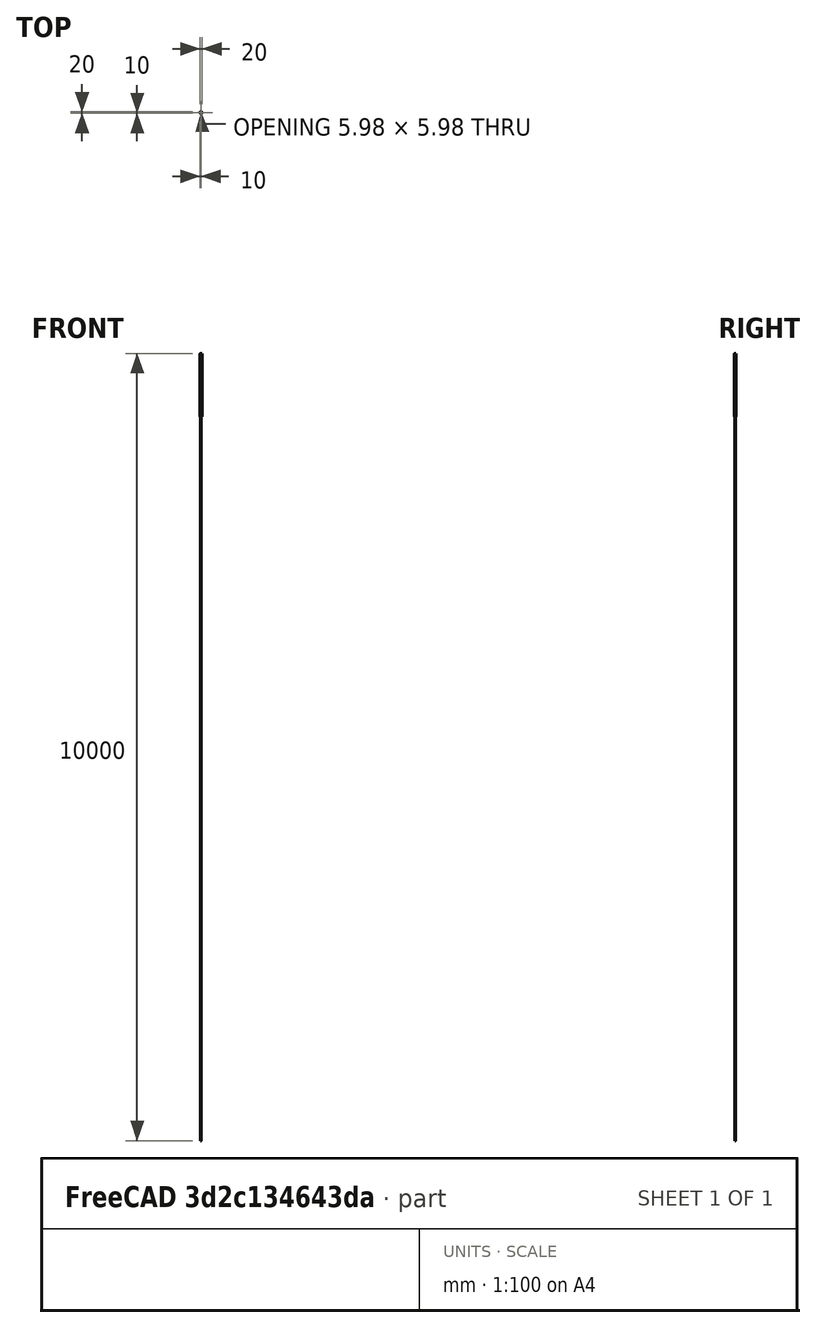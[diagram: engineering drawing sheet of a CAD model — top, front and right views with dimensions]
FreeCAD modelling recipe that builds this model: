
FCSTD DOCUMENT  (FreeCAD 0.14R3703 (Git))
Label: perfiles_verticales
License: CC-BY 3.0
LicenseURL: http://creativecommons.org/licenses/by/3.0/
objects: Sketcher::SketchObject×2, PartDesign::Pad×1, PartDesign::Pocket×1, Part::Feature×1
note: 7 computed .brp shape members not serialized (recipe doc carries the construction recipe); baked Part::Feature solids carry a one-line shape summary decoded from their .brp

FEATURE [Sketcher::SketchObject] Sketch
  Placement = pos=(1.5,0,0) rot=(0,0,1;0rad)
  sketch-geometry (136):
    g0: LineSegment StartX=0 StartY=20 StartZ=0 EndX=4.65 EndY=20 EndZ=0
    g1: ArcOfCircle CenterX=-1e-12 CenterY=18.5 CenterZ=0 NormalX=0 NormalY=0 NormalZ=1 Radius=1.5 StartAngle=1.5708 EndAngle=3.14159
    g2: LineSegment StartX=-1.5 StartY=13.85 StartZ=0 EndX=-1.5 EndY=18.5 EndZ=0
    g3: ArcOfCircle CenterX=-1.3 CenterY=13.85 CenterZ=0 NormalX=0 NormalY=0 NormalZ=1 Radius=0.2 StartAngle=3.14159 EndAngle=4.71239
    g4: LineSegment StartX=-1 StartY=13.65 StartZ=0 EndX=-1.3 EndY=13.65 EndZ=0
    g5: LineSegment StartX=-1 StartY=13.3 StartZ=0 EndX=-1 EndY=13.65 EndZ=0
    g6: ArcOfCircle CenterX=-0.8 CenterY=13.3 CenterZ=0 NormalX=0 NormalY=0 NormalZ=1 Radius=0.2 StartAngle=3.14159 EndAngle=4.71239
    g7: LineSegment StartX=-0.5 StartY=13.1 StartZ=0 EndX=-0.8 EndY=13.1 EndZ=0
    g8: ArcOfCircle CenterX=-0.5 CenterY=13.6 CenterZ=0 NormalX=0 NormalY=0 NormalZ=1 Radius=0.5 StartAngle=4.71239 EndAngle=6.28319
    g9: LineSegment StartX=2.68e-07 StartY=15.5 StartZ=0 EndX=2.68e-07 EndY=13.6 EndZ=0
    g10: ArcOfCircle CenterX=0.5 CenterY=15.5 CenterZ=0 NormalX=0 NormalY=0 NormalZ=1 Radius=0.5 StartAngle=1.5708 EndAngle=3.14159
    g11: LineSegment StartX=1.23223 StartY=16 StartZ=0 EndX=0.5 EndY=16 EndZ=0
    g12: ArcOfCircle CenterX=1.23223 CenterY=15.5 CenterZ=0 NormalX=0 NormalY=0 NormalZ=1 Radius=0.5 StartAngle=0.785398 EndAngle=1.5708
    g13: LineSegment StartX=3.85355 StartY=13.5858 StartZ=0 EndX=1.58579 EndY=15.8536 EndZ=0
    g14: ArcOfCircle CenterX=3.5 CenterY=13.2322 CenterZ=0 NormalX=0 NormalY=0 NormalZ=1 Radius=0.5 StartAngle=0 EndAngle=0.785398
    g15: LineSegment StartX=4 StartY=10.9536 StartZ=0 EndX=4 EndY=13.2322 EndZ=0
    g16: ArcOfCircle CenterX=4.2 CenterY=10.9536 CenterZ=0 NormalX=0 NormalY=0 NormalZ=1 Radius=0.2 StartAngle=3.14159 EndAngle=3.66519
    g17: LineSegment StartX=4.46188 StartY=10.1 StartZ=0 EndX=4.0268 EndY=10.8536 EndZ=0
    g18: ArcOfCircle CenterX=4.28868 CenterY=10 CenterZ=0 NormalX=0 NormalY=0 NormalZ=1 Radius=0.2 StartAngle=5.75959 EndAngle=6.80678
    g19: LineSegment StartX=4.0268 StartY=9.14641 StartZ=0 EndX=4.46188 EndY=9.9 EndZ=0
    g20: ArcOfCircle CenterX=4.2 CenterY=9.04641 CenterZ=0 NormalX=0 NormalY=0 NormalZ=1 Radius=0.2 StartAngle=2.61799 EndAngle=3.14159
    g21: LineSegment StartX=4 StartY=6.76777 StartZ=0 EndX=4 EndY=9.04641 EndZ=0
    g22: ArcOfCircle CenterX=3.5 CenterY=6.76777 CenterZ=0 NormalX=0 NormalY=0 NormalZ=1 Radius=0.5 StartAngle=5.49779 EndAngle=6.28319
    g23: LineSegment StartX=1.58579 StartY=4.14645 StartZ=0 EndX=3.85355 EndY=6.41421 EndZ=0
    g24: ArcOfCircle CenterX=1.23223 CenterY=4.5 CenterZ=0 NormalX=0 NormalY=0 NormalZ=1 Radius=0.5 StartAngle=4.71239 EndAngle=5.49779
    g25: LineSegment StartX=0.5 StartY=4 StartZ=0 EndX=1.23223 EndY=4 EndZ=0
    g26: ArcOfCircle CenterX=0.5 CenterY=4.5 CenterZ=0 NormalX=0 NormalY=0 NormalZ=1 Radius=0.5 StartAngle=3.14159 EndAngle=4.71239
    g27: LineSegment StartX=2.68e-07 StartY=6.4 StartZ=0 EndX=2.68e-07 EndY=4.5 EndZ=0
    g28: ArcOfCircle CenterX=-0.5 CenterY=6.4 CenterZ=0 NormalX=0 NormalY=0 NormalZ=1 Radius=0.5 StartAngle=0 EndAngle=1.5708
    g29: LineSegment StartX=-0.8 StartY=6.9 StartZ=0 EndX=-0.5 EndY=6.9 EndZ=0
    g30: ArcOfCircle CenterX=-0.8 CenterY=6.7 CenterZ=0 NormalX=0 NormalY=0 NormalZ=1 Radius=0.2 StartAngle=1.5708 EndAngle=3.14159
    g31: LineSegment StartX=-1 StartY=6.35 StartZ=0 EndX=-1 EndY=6.7 EndZ=0
    g32: LineSegment StartX=-1.3 StartY=6.35 StartZ=0 EndX=-1 EndY=6.35 EndZ=0
    g33: ArcOfCircle CenterX=-1.3 CenterY=6.15 CenterZ=0 NormalX=0 NormalY=0 NormalZ=1 Radius=0.2 StartAngle=1.5708 EndAngle=3.14159
    g34: LineSegment StartX=-1.5 StartY=1.5 StartZ=0 EndX=-1.5 EndY=6.15 EndZ=0
    g35: ArcOfCircle CenterX=0 CenterY=1.5 CenterZ=0 NormalX=0 NormalY=0 NormalZ=1 Radius=1.5 StartAngle=3.14159 EndAngle=4.71239
    g36: LineSegment StartX=4.65 StartY=1e-12 StartZ=0 EndX=0 EndY=0 EndZ=0
    g37: ArcOfCircle CenterX=4.65 CenterY=0.2 CenterZ=0 NormalX=0 NormalY=0 NormalZ=1 Radius=0.2 StartAngle=4.71239 EndAngle=6.28319
    g38: LineSegment StartX=4.85 StartY=0.5 StartZ=0 EndX=4.85 EndY=0.2 EndZ=0
    g39: LineSegment StartX=5.2 StartY=0.5 StartZ=0 EndX=4.85 EndY=0.5 EndZ=0
    g40: ArcOfCircle CenterX=5.2 CenterY=0.7 CenterZ=0 NormalX=0 NormalY=0 NormalZ=1 Radius=0.2 StartAngle=4.71239 EndAngle=6.28319
    g41: LineSegment StartX=5.4 StartY=1 StartZ=0 EndX=5.4 EndY=0.7 EndZ=0
    g42: ArcOfCircle CenterX=4.9 CenterY=1 CenterZ=0 NormalX=0 NormalY=0 NormalZ=1 Radius=0.5 StartAngle=0 EndAngle=1.5708
    g43: LineSegment StartX=3 StartY=1.5 StartZ=0 EndX=4.9 EndY=1.5 EndZ=0
    g44: ArcOfCircle CenterX=3 CenterY=2 CenterZ=0 NormalX=0 NormalY=0 NormalZ=1 Radius=0.5 StartAngle=3.14159 EndAngle=4.71239
    g45: LineSegment StartX=2.5 StartY=2.73223 StartZ=0 EndX=2.5 EndY=2 EndZ=0
    g46: ArcOfCircle CenterX=3 CenterY=2.73223 CenterZ=0 NormalX=0 NormalY=0 NormalZ=1 Radius=0.5 StartAngle=2.35619 EndAngle=3.14159
    g47: LineSegment StartX=4.91421 StartY=5.35355 StartZ=0 EndX=2.64645 EndY=3.08579 EndZ=0
    g48: ArcOfCircle CenterX=5.26777 CenterY=5 CenterZ=0 NormalX=0 NormalY=0 NormalZ=1 Radius=0.5 StartAngle=1.5708 EndAngle=2.35619
    g49: LineSegment StartX=7.54641 StartY=5.5 StartZ=0 EndX=5.26777 EndY=5.5 EndZ=0
    g50: ArcOfCircle CenterX=7.54641 CenterY=5.7 CenterZ=0 NormalX=0 NormalY=0 NormalZ=1 Radius=0.2 StartAngle=4.71239 EndAngle=5.23599
    g51: LineSegment StartX=8.4 StartY=5.96188 StartZ=0 EndX=7.64641 EndY=5.52679 EndZ=0
    g52: ArcOfCircle CenterX=8.5 CenterY=5.78868 CenterZ=0 NormalX=0 NormalY=0 NormalZ=1 Radius=0.2 StartAngle=1.0472 EndAngle=2.0944
    g53: LineSegment StartX=9.35359 StartY=5.52679 StartZ=0 EndX=8.6 EndY=5.96188 EndZ=0
    g54: ArcOfCircle CenterX=9.45359 CenterY=5.7 CenterZ=0 NormalX=0 NormalY=0 NormalZ=1 Radius=0.2 StartAngle=4.18879 EndAngle=4.71239
    g55: LineSegment StartX=11.7322 StartY=5.5 StartZ=0 EndX=9.45359 EndY=5.5 EndZ=0
    g56: ArcOfCircle CenterX=11.7322 CenterY=5 CenterZ=0 NormalX=0 NormalY=0 NormalZ=1 Radius=0.5 StartAngle=0.785398 EndAngle=1.5708
    g57: LineSegment StartX=14.3536 StartY=3.08579 StartZ=0 EndX=12.0858 EndY=5.35355 EndZ=0
    g58: ArcOfCircle CenterX=14 CenterY=2.73223 CenterZ=0 NormalX=0 NormalY=0 NormalZ=1 Radius=0.5 StartAngle=0 EndAngle=0.785398
    g59: LineSegment StartX=14.5 StartY=2 StartZ=0 EndX=14.5 EndY=2.73223 EndZ=0
    g60: ArcOfCircle CenterX=14 CenterY=2 CenterZ=0 NormalX=0 NormalY=0 NormalZ=1 Radius=0.5 StartAngle=4.71239 EndAngle=6.28319
    g61: LineSegment StartX=12.1 StartY=1.5 StartZ=0 EndX=14 EndY=1.5 EndZ=0
    g62: ArcOfCircle CenterX=12.1 CenterY=1 CenterZ=0 NormalX=0 NormalY=0 NormalZ=1 Radius=0.5 StartAngle=1.5708 EndAngle=3.14159
    g63: LineSegment StartX=11.6 StartY=0.7 StartZ=0 EndX=11.6 EndY=1 EndZ=0
    g64: ArcOfCircle CenterX=11.8 CenterY=0.7 CenterZ=0 NormalX=0 NormalY=0 NormalZ=1 Radius=0.2 StartAngle=3.14159 EndAngle=4.71239
    g65: LineSegment StartX=12.15 StartY=0.5 StartZ=0 EndX=11.8 EndY=0.5 EndZ=0
    g66: LineSegment StartX=12.15 StartY=0.2 StartZ=0 EndX=12.15 EndY=0.5 EndZ=0
    g67: ArcOfCircle CenterX=12.35 CenterY=0.2 CenterZ=0 NormalX=0 NormalY=0 NormalZ=1 Radius=0.2 StartAngle=3.14159 EndAngle=4.71239
    g68: LineSegment StartX=17 StartY=1e-12 StartZ=0 EndX=12.35 EndY=0 EndZ=0
    g69: ArcOfCircle CenterX=17 CenterY=1.5 CenterZ=0 NormalX=0 NormalY=0 NormalZ=1 Radius=1.5 StartAngle=4.71239 EndAngle=6.28319
    g70: LineSegment StartX=18.5 StartY=6.15 StartZ=0 EndX=18.5 EndY=1.5 EndZ=0
    g71: ArcOfCircle CenterX=18.3 CenterY=6.15 CenterZ=0 NormalX=0 NormalY=0 NormalZ=1 Radius=0.2 StartAngle=0 EndAngle=1.5708
    g72: LineSegment StartX=18 StartY=6.35 StartZ=0 EndX=18.3 EndY=6.35 EndZ=0
    g73: LineSegment StartX=18 StartY=6.7 StartZ=0 EndX=18 EndY=6.35 EndZ=0
    g74: ArcOfCircle CenterX=17.8 CenterY=6.7 CenterZ=0 NormalX=0 NormalY=0 NormalZ=1 Radius=0.2 StartAngle=0 EndAngle=1.5708
    g75: LineSegment StartX=17.5 StartY=6.9 StartZ=0 EndX=17.8 EndY=6.9 EndZ=0
    g76: ArcOfCircle CenterX=17.5 CenterY=6.4 CenterZ=0 NormalX=0 NormalY=0 NormalZ=1 Radius=0.5 StartAngle=1.5708 EndAngle=3.14159
    g77: LineSegment StartX=17 StartY=4.5 StartZ=0 EndX=17 EndY=6.4 EndZ=0
    g78: ArcOfCircle CenterX=16.5 CenterY=4.5 CenterZ=0 NormalX=0 NormalY=0 NormalZ=1 Radius=0.5 StartAngle=4.71239 EndAngle=6.28319
    g79: LineSegment StartX=15.7678 StartY=4 StartZ=0 EndX=16.5 EndY=4 EndZ=0
    g80: ArcOfCircle CenterX=15.7678 CenterY=4.5 CenterZ=0 NormalX=0 NormalY=0 NormalZ=1 Radius=0.5 StartAngle=3.92699 EndAngle=4.71239
    g81: LineSegment StartX=13.1464 StartY=6.41421 StartZ=0 EndX=15.4142 EndY=4.14645 EndZ=0
    g82: ArcOfCircle CenterX=13.5 CenterY=6.76777 CenterZ=0 NormalX=0 NormalY=0 NormalZ=1 Radius=0.5 StartAngle=3.14159 EndAngle=3.92699
    g83: LineSegment StartX=13 StartY=9.04641 StartZ=0 EndX=13 EndY=6.76777 EndZ=0
    g84: ArcOfCircle CenterX=12.8 CenterY=9.04641 CenterZ=0 NormalX=0 NormalY=0 NormalZ=1 Radius=0.2 StartAngle=0 EndAngle=0.523599
    g85: LineSegment StartX=12.5381 StartY=9.9 StartZ=0 EndX=12.9732 EndY=9.14641 EndZ=0
    g86: ArcOfCircle CenterX=12.7113 CenterY=10 CenterZ=0 NormalX=0 NormalY=0 NormalZ=1 Radius=0.2 StartAngle=2.61799 EndAngle=3.66519
    g87: LineSegment StartX=12.9732 StartY=10.8536 StartZ=0 EndX=12.5381 EndY=10.1 EndZ=0
    g88: ArcOfCircle CenterX=12.8 CenterY=10.9536 CenterZ=0 NormalX=0 NormalY=0 NormalZ=1 Radius=0.2 StartAngle=5.75959 EndAngle=6.28319
    g89: LineSegment StartX=13 StartY=13.2322 StartZ=0 EndX=13 EndY=10.9536 EndZ=0
    g90: ArcOfCircle CenterX=13.5 CenterY=13.2322 CenterZ=0 NormalX=0 NormalY=0 NormalZ=1 Radius=0.5 StartAngle=2.35619 EndAngle=3.14159
    g91: LineSegment StartX=15.4142 StartY=15.8536 StartZ=0 EndX=13.1464 EndY=13.5858 EndZ=0
    g92: ArcOfCircle CenterX=15.7678 CenterY=15.5 CenterZ=0 NormalX=0 NormalY=0 NormalZ=1 Radius=0.5 StartAngle=1.5708 EndAngle=2.35619
    g93: LineSegment StartX=16.5 StartY=16 StartZ=0 EndX=15.7678 EndY=16 EndZ=0
    g94: ArcOfCircle CenterX=16.5 CenterY=15.5 CenterZ=0 NormalX=0 NormalY=0 NormalZ=1 Radius=0.5 StartAngle=0 EndAngle=1.5708
    g95: LineSegment StartX=17 StartY=13.6 StartZ=0 EndX=17 EndY=15.5 EndZ=0
    g96: ArcOfCircle CenterX=17.5 CenterY=13.6 CenterZ=0 NormalX=0 NormalY=0 NormalZ=1 Radius=0.5 StartAngle=3.14159 EndAngle=4.71239
    g97: LineSegment StartX=17.8 StartY=13.1 StartZ=0 EndX=17.5 EndY=13.1 EndZ=0
    g98: ArcOfCircle CenterX=17.8 CenterY=13.3 CenterZ=0 NormalX=0 NormalY=0 NormalZ=1 Radius=0.2 StartAngle=4.71239 EndAngle=6.28319
    g99: LineSegment StartX=18 StartY=13.65 StartZ=0 EndX=18 EndY=13.3 EndZ=0
    g100: LineSegment StartX=18.3 StartY=13.65 StartZ=0 EndX=18 EndY=13.65 EndZ=0
    g101: ArcOfCircle CenterX=18.3 CenterY=13.85 CenterZ=0 NormalX=0 NormalY=0 NormalZ=1 Radius=0.2 StartAngle=4.71239 EndAngle=6.28319
    g102: LineSegment StartX=18.5 StartY=18.5 StartZ=0 EndX=18.5 EndY=13.85 EndZ=0
    g103: ArcOfCircle CenterX=17 CenterY=18.5 CenterZ=0 NormalX=0 NormalY=0 NormalZ=1 Radius=1.5 StartAngle=0 EndAngle=1.5708
    g104: LineSegment StartX=12.35 StartY=20 StartZ=0 EndX=17 EndY=20 EndZ=0
    g105: ArcOfCircle CenterX=12.35 CenterY=19.8 CenterZ=0 NormalX=0 NormalY=0 NormalZ=1 Radius=0.2 StartAngle=1.5708 EndAngle=3.14159
    g106: LineSegment StartX=12.15 StartY=19.5 StartZ=0 EndX=12.15 EndY=19.8 EndZ=0
    g107: LineSegment StartX=11.8 StartY=19.5 StartZ=0 EndX=12.15 EndY=19.5 EndZ=0
    g108: ArcOfCircle CenterX=11.8 CenterY=19.3 CenterZ=0 NormalX=0 NormalY=0 NormalZ=1 Radius=0.2 StartAngle=1.5708 EndAngle=3.14159
    g109: LineSegment StartX=11.6 StartY=19 StartZ=0 EndX=11.6 EndY=19.3 EndZ=0
    g110: ArcOfCircle CenterX=12.1 CenterY=19 CenterZ=0 NormalX=0 NormalY=0 NormalZ=1 Radius=0.5 StartAngle=3.14159 EndAngle=4.71239
    g111: LineSegment StartX=14 StartY=18.5 StartZ=0 EndX=12.1 EndY=18.5 EndZ=0
    g112: ArcOfCircle CenterX=14 CenterY=18 CenterZ=0 NormalX=0 NormalY=0 NormalZ=1 Radius=0.5 StartAngle=0 EndAngle=1.5708
    g113: LineSegment StartX=14.5 StartY=17.2678 StartZ=0 EndX=14.5 EndY=18 EndZ=0
    g114: ArcOfCircle CenterX=14 CenterY=17.2678 CenterZ=0 NormalX=0 NormalY=0 NormalZ=1 Radius=0.5 StartAngle=5.49779 EndAngle=6.28319
    g115: LineSegment StartX=12.0858 StartY=14.6464 StartZ=0 EndX=14.3536 EndY=16.9142 EndZ=0
    g116: ArcOfCircle CenterX=11.7322 CenterY=15 CenterZ=0 NormalX=0 NormalY=0 NormalZ=1 Radius=0.5 StartAngle=4.71239 EndAngle=5.49779
    g117: LineSegment StartX=9.45359 StartY=14.5 StartZ=0 EndX=11.7322 EndY=14.5 EndZ=0
    g118: ArcOfCircle CenterX=9.45359 CenterY=14.3 CenterZ=0 NormalX=0 NormalY=0 NormalZ=1 Radius=0.2 StartAngle=1.5708 EndAngle=2.0944
    g119: LineSegment StartX=8.6 StartY=14.0381 StartZ=0 EndX=9.35359 EndY=14.4732 EndZ=0
    g120: ArcOfCircle CenterX=8.5 CenterY=14.2113 CenterZ=0 NormalX=0 NormalY=0 NormalZ=1 Radius=0.2 StartAngle=4.18879 EndAngle=5.23599
    g121: LineSegment StartX=7.64641 StartY=14.4732 StartZ=0 EndX=8.4 EndY=14.0381 EndZ=0
    g122: ArcOfCircle CenterX=7.54641 CenterY=14.3 CenterZ=0 NormalX=0 NormalY=0 NormalZ=1 Radius=0.2 StartAngle=1.0472 EndAngle=1.5708
    g123: LineSegment StartX=5.26777 StartY=14.5 StartZ=0 EndX=7.54641 EndY=14.5 EndZ=0
    g124: ArcOfCircle CenterX=5.26777 CenterY=15 CenterZ=0 NormalX=0 NormalY=0 NormalZ=1 Radius=0.5 StartAngle=3.92699 EndAngle=4.71239
    g125: LineSegment StartX=2.64645 StartY=16.9142 StartZ=0 EndX=4.91421 EndY=14.6464 EndZ=0
    g126: ArcOfCircle CenterX=3 CenterY=17.2678 CenterZ=0 NormalX=0 NormalY=0 NormalZ=1 Radius=0.5 StartAngle=3.14159 EndAngle=3.92699
    g127: LineSegment StartX=2.5 StartY=18 StartZ=0 EndX=2.5 EndY=17.2678 EndZ=0
    g128: ArcOfCircle CenterX=3 CenterY=18 CenterZ=0 NormalX=0 NormalY=0 NormalZ=1 Radius=0.5 StartAngle=1.5708 EndAngle=3.14159
    g129: LineSegment StartX=4.9 StartY=18.5 StartZ=0 EndX=3 EndY=18.5 EndZ=0
    g130: ArcOfCircle CenterX=4.9 CenterY=19 CenterZ=0 NormalX=0 NormalY=0 NormalZ=1 Radius=0.5 StartAngle=4.71239 EndAngle=6.28319
    g131: LineSegment StartX=5.4 StartY=19.3 StartZ=0 EndX=5.4 EndY=19 EndZ=0
    g132: ArcOfCircle CenterX=5.2 CenterY=19.3 CenterZ=0 NormalX=0 NormalY=0 NormalZ=1 Radius=0.2 StartAngle=0 EndAngle=1.5708
    g133: LineSegment StartX=4.85 StartY=19.5 StartZ=0 EndX=5.2 EndY=19.5 EndZ=0
    g134: LineSegment StartX=4.85 StartY=19.8 StartZ=0 EndX=4.85 EndY=19.5 EndZ=0
    g135: ArcOfCircle CenterX=4.65 CenterY=19.8 CenterZ=0 NormalX=0 NormalY=0 NormalZ=1 Radius=0.2 StartAngle=0 EndAngle=1.5708
  constraints (136):
    c: Coincident(g0,g1)
    c: Coincident(g135,g0)
    c: Coincident(g1,g2)
    c: Coincident(g2,g3)
    c: Coincident(g3,g4)
    c: Coincident(g4,g5)
    c: Coincident(g6,g5)
    c: Coincident(g7,g6)
    c: Coincident(g8,g7)
    c: Coincident(g9,g8)
    c: Coincident(g10,g9)
    c: Coincident(g10,g11)
    c: Coincident(g11,g12)
    c: Coincident(g12,g13)
    c: Coincident(g14,g13)
    c: Coincident(g15,g14)
    c: Coincident(g15,g16)
    c: Coincident(g16,g17)
    c: Coincident(g17,g18)
    c: Coincident(g18,g19)
    c: Coincident(g19,g20)
    c: Coincident(g20,g21)
    c: Coincident(g21,g22)
    c: Coincident(g22,g23)
    c: Coincident(g23,g24)
    c: Coincident(g24,g25)
    c: Coincident(g26,g25)
    c: Coincident(g26,g27)
    c: Coincident(g28,g27)
    c: Coincident(g28,g29)
    c: Coincident(g30,g29)
    c: Coincident(g31,g30)
    c: Coincident(g31,g32)
    c: Coincident(g32,g33)
    c: Coincident(g33,g34)
    c: Coincident(g35,g34)
    c: Coincident(g36,g35)
    c: Coincident(g37,g36)
    c: Coincident(g37,g38)
    c: Coincident(g38,g39)
    c: Coincident(g40,g39)
    c: Coincident(g40,g41)
    c: Coincident(g41,g42)
    c: Coincident(g43,g42)
    c: Coincident(g44,g43)
    c: Coincident(g44,g45)
    c: Coincident(g45,g46)
    c: Coincident(g46,g47)
    c: Coincident(g47,g48)
    c: Coincident(g49,g48)
    c: Coincident(g49,g50)
    c: Coincident(g50,g51)
    c: Coincident(g51,g52)
    c: Coincident(g53,g52)
    c: Coincident(g54,g53)
    c: Coincident(g55,g54)
    c: Coincident(g56,g55)
    c: Coincident(g56,g57)
    c: Coincident(g58,g57)
    c: Coincident(g59,g58)
    c: Coincident(g60,g59)
    c: Coincident(g61,g60)
    c: Coincident(g62,g61)
    c: Coincident(g62,g63)
    c: Coincident(g64,g63)
    c: Coincident(g65,g64)
    c: Coincident(g66,g65)
    c: Coincident(g67,g66)
    c: Coincident(g67,g68)
    c: Coincident(g69,g68)
    c: Coincident(g70,g69)
    c: Coincident(g71,g70)
    c: Coincident(g72,g71)
    c: Coincident(g73,g72)
    c: Coincident(g73,g74)
    c: Coincident(g75,g74)
    c: Coincident(g76,g75)
    c: Coincident(g76,g77)
    c: Coincident(g77,g78)
    c: Coincident(g78,g79)
    c: Coincident(g80,g79)
    c: Coincident(g81,g80)
    c: Coincident(g81,g82)
    c: Coincident(g82,g83)
    c: Coincident(g83,g84)
    c: Coincident(g85,g84)
    c: Coincident(g86,g85)
    c: Coincident(g86,g87)
    c: Coincident(g88,g87)
    c: Coincident(g88,g89)
    c: Coincident(g89,g90)
    c: Coincident(g91,g90)
    c: Coincident(g92,g91)
    c: Coincident(g93,g92)
    c: Coincident(g94,g93)
    c: Coincident(g94,g95)
    c: Coincident(g95,g96)
    c: Coincident(g96,g97)
    c: Coincident(g98,g97)
    c: Coincident(g98,g99)
    c: Coincident(g100,g99)
    c: Coincident(g100,g101)
    c: Coincident(g101,g102)
    c: Coincident(g102,g103)
    c: Coincident(g103,g104)
    c: Coincident(g104,g105)
    c: Coincident(g106,g105)
    c: Coincident(g107,g106)
    c: Coincident(g108,g107)
    c: Coincident(g109,g108)
    c: Coincident(g110,g109)
    c: Coincident(g111,g110)
    c: Coincident(g112,g111)
    c: Coincident(g112,g113)
    c: Coincident(g113,g114)
    c: Coincident(g114,g115)
    c: Coincident(g115,g116)
    c: Coincident(g117,g116)
    c: Coincident(g118,g117)
    c: Coincident(g119,g118)
    c: Coincident(g119,g120)
    c: Coincident(g121,g120)
    c: Coincident(g121,g122)
    c: Coincident(g122,g123)
    c: Coincident(g124,g123)
    c: Coincident(g124,g125)
    c: Coincident(g126,g125)
    c: Coincident(g127,g126)
    c: Coincident(g128,g127)
    c: Coincident(g129,g128)
    c: Coincident(g130,g129)
    c: Coincident(g130,g131)
    c: Coincident(g131,g132)
    c: Coincident(g133,g132)
    c: Coincident(g134,g133)
    c: Coincident(g135,g134)
FEATURE [PartDesign::Pad] Pad
  Length = 800
  Length2 = 100
  Placement = pos=(1.5,0,0) rot=(0,0,1;0rad)
  Sketch = -> Sketch
  Type = 0
FEATURE [Sketcher::SketchObject] Sketch001
  Placement = pos=(1.5,0,800) rot=(0,0,1;0rad)
  Support = -> Pad [Face138]
  sketch-geometry (16):
    g0: ArcOfCircle CenterX=8.5 CenterY=10 CenterZ=0 NormalX=0 NormalY=0 NormalZ=1 Radius=3.54978 StartAngle=2.14023 EndAngle=2.57348
    g1: LineSegment StartX=6.5861 StartY=12.9896 StartZ=0 EndX=7.24181 EndY=12.4453 EndZ=0
    g2: ArcOfCircle CenterX=8.5 CenterY=10 CenterZ=0 NormalX=0 NormalY=0 NormalZ=1 Radius=2.75 StartAngle=1.09559 EndAngle=2.046
    g3: LineSegment StartX=9.75819 StartY=12.4453 StartZ=0 EndX=10.4139 EndY=12.9896 EndZ=0
    g4: ArcOfCircle CenterX=8.5 CenterY=10 CenterZ=0 NormalX=0 NormalY=0 NormalZ=1 Radius=3.54978 StartAngle=0.568112 EndAngle=1.00136
    g5: LineSegment StartX=11.4922 StartY=11.9099 StartZ=0 EndX=10.9453 EndY=11.2582 EndZ=0
    g6: ArcOfCircle CenterX=8.5 CenterY=10 CenterZ=0 NormalX=0 NormalY=0 NormalZ=1 Radius=2.75 StartAngle=5.80798 EndAngle=6.75839
    g7: LineSegment StartX=10.9453 StartY=8.74181 StartZ=0 EndX=11.4922 EndY=8.09007 EndZ=0
    g8: ArcOfCircle CenterX=8.5 CenterY=10 CenterZ=0 NormalX=0 NormalY=0 NormalZ=1 Radius=3.54978 StartAngle=5.28183 EndAngle=5.71507
    g9: LineSegment StartX=10.4139 StartY=7.01036 StartZ=0 EndX=9.75819 EndY=7.5547 EndZ=0
    g10: ArcOfCircle CenterX=8.5 CenterY=10 CenterZ=0 NormalX=0 NormalY=0 NormalZ=1 Radius=2.75 StartAngle=4.23718 EndAngle=5.1876
    g11: LineSegment StartX=7.24181 StartY=7.5547 StartZ=0 EndX=6.5861 EndY=7.01036 EndZ=0
    g12: ArcOfCircle CenterX=8.5 CenterY=10 CenterZ=0 NormalX=0 NormalY=0 NormalZ=1 Radius=3.54978 StartAngle=3.7097 EndAngle=4.14295
    g13: LineSegment StartX=5.50783 StartY=8.09007 StartZ=0 EndX=6.0547 EndY=8.74181 EndZ=0
    g14: ArcOfCircle CenterX=8.5 CenterY=10 CenterZ=0 NormalX=0 NormalY=0 NormalZ=1 Radius=2.75 StartAngle=2.66639 EndAngle=3.6168
    g15: LineSegment StartX=6.0547 StartY=11.2582 StartZ=0 EndX=5.50783 EndY=11.9099 EndZ=0
  constraints (16):
    c: Coincident(g0,g1)
    c: Coincident(g15,g0)
    c: Coincident(g1,g2)
    c: Coincident(g3,g2)
    c: Coincident(g4,g3)
    c: Coincident(g4,g5)
    c: Coincident(g6,g5)
    c: Coincident(g7,g6)
    c: Coincident(g8,g7)
    c: Coincident(g9,g8)
    c: Coincident(g10,g9)
    c: Coincident(g11,g10)
    c: Coincident(g12,g11)
    c: Coincident(g13,g12)
    c: Coincident(g14,g13)
    c: Coincident(g15,g14)
FEATURE [PartDesign::Pocket] Pocket
  Length = 5
  Placement = pos=(1.5,0,0) rot=(0,0,1;0rad)
  Sketch = -> Sketch001
  Type = 1
FEATURE [Part::Feature] Pocket001  label="perfiles_verticales"
  Placement = pos=(1.5,0,0) rot=(0,0,1;0rad)
  shape: bbox 20 x 20 x 800 mm, 154 faces (baked)
